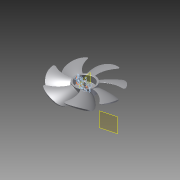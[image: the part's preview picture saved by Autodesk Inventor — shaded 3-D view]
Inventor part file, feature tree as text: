
AUTODESK INVENTOR PART (.ipt)
format: ipt  version: 2011 SP2 (Build 150309200, 309)  size: 1,067,520 bytes
history: native  units: mm
features: sketch x7, fillet x3, revolve x3, plane x2, extrude x2, loft x1, pattern_circular x1, chamfer x1
ambient origin geometry x8: Origin, YZ Plane, XZ Plane, XY Plane, X Axis, Y Axis, Z Axis, Center Point
bodies: Solid1 (feature_tree), Solid2 (feature_tree)
feature tree (20):
  sketch  "Sketch1"  dims[d0=10.0mm d1=15.0deg]
  plane  "Work Plane1"
  plane  "Work Plane2"
  loft  "Loft1"
  extrude  "Extrusion1"  TaperAngle=90.0deg  [1 undecoded]
  fillet  "Fillet1"  Radius=15.0mm
  pattern_circular  "Circular Pattern1"  Count=20  [1 undecoded]
  extrude  "Extrusion2"  Depth=100.0mm
  revolve  "Revolution1"  Angle=90.0deg
  fillet  "Fillet2"  [1 undecoded]
  fillet  "Fillet3"  [1 undecoded]
  sketch  "Sketch7"  dims[d11=15.0deg d12=100.0mm d13=0.0mm d14=90.0deg d15=0.0mm d16=90.0deg d17=0.0mm d18=90.0deg d19=45.0mm d23=2.0mm d24=12.0mm d25=45.0deg d26=10.0mm d27=0.0mm d28=0.5mm d29=0.0mm d30=0.5mm d31=0.0mm d32=70.0mm d33=360.0deg d35=15.0mm d36=6.0mm d37=5.5mm d38=0.0mm d39=0.0mm d40=3.25mm d41=2.5mm d42=12.5mm d43=6.0mm d44=90.0deg d45=0.5mm d46=0.5mm d47=1.5mm d48=0.5mm d49=1.0mm d51=2.0mm d52=0.5mm d53=0.75mm d54=2.0mm d55=11.0mm d56=2.0mm d57=8.0mm d58=90.0deg d59=90.0deg d60=0.5mm d61=2.0mm d62=45.0deg]
  revolve  "Revolution2"  [1 undecoded]
  revolve  "Revolution3"  [1 undecoded]
  chamfer  "Chamfer1"  Distance=12.0mm
  sketch  "Sketch2"  dims[d2=45.0mm d3=90.0deg d4=15.0mm]
  sketch  "Sketch3"  dims[d5=45.0deg]
  sketch  "Sketch4"  dims[d6=10.0mm]
  sketch  "Sketch5"  dims[d7=45.0mm]
  sketch  "Sketch6"  dims[d8=45.0mm d9=200.0mm]
note: 6 required parameter values undecoded (feature->parameter linkage not recoverable at this tier; creation-order binding heuristic only, values carry confidence <= 0.55)